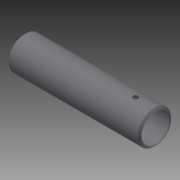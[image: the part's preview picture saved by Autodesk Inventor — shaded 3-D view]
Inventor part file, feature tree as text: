
AUTODESK INVENTOR PART (.ipt)
format: ipt  version: 2014 (Build 180170000, 170)  size: 133,120 bytes
history: native  units: in
note: dims shown in document units (in); Inventor stores cm internally (conversion verified against a paired STEP export)
features: other x56, revolve x2, sketch x2
ambient origin geometry x8: Origin, YZ Plane, XZ Plane, XY Plane, X Axis, Y Axis, Z Axis, Center Point
bodies: Solid1 (feature_tree)
feature tree (60):
  revolve  "Revolution1"  Angle=360.0deg
  revolve  "Revolution2"  [1 undecoded]
  other  "o1_XY"
  other  "o1_YZ"
  other  "o1_ZX"
  other  "o1_X"
  other  "o1_Y"
  other  "o1_Z"
  other  "o1_Center"
  other  "o2_XY"
  other  "o2_YZ"
  other  "o2_ZX"
  other  "o2_X"
  other  "o2_Y"
  other  "o2_Z"
  other  "o2_Center"
  other  "t1_XY"
  other  "t1_YZ"
  other  "t1_ZX"
  other  "t1_X"
  other  "t1_Y"
  other  "t1_Z"
  other  "t1_Center"
  other  "t2_XY"
  other  "t2_YZ"
  other  "t2_ZX"
  other  "t2_X"
  other  "t2_Y"
  other  "t2_Z"
  other  "t2_Center"
  other  "t3_XY"
  other  "t3_YZ"
  other  "t3_ZX"
  other  "t3_X"
  other  "t3_Y"
  other  "t3_Z"
  other  "t3_Center"
  other  "t4_XY"
  other  "t4_YZ"
  other  "t4_ZX"
  other  "t4_X"
  other  "t4_Y"
  other  "t4_Z"
  other  "t4_Center"
  other  "tube1_XY"
  other  "tube1_YZ"
  other  "tube1_ZX"
  other  "tube1_X"
  other  "tube1_Y"
  other  "tube1_Z"
  other  "tube1_Center"
  other  "tube2_XY"
  other  "tube2_YZ"
  other  "tube2_ZX"
  other  "tube2_X"
  other  "tube2_Y"
  other  "tube2_Z"
  other  "tube2_Center"
  sketch  "Sketch_5"
  sketch  "Sketch_1"  dims[d0=360.0deg d1=360.0deg]
note: 1 required parameter value undecoded (feature->parameter linkage not recoverable at this tier; creation-order binding heuristic only, values carry confidence <= 0.55)
